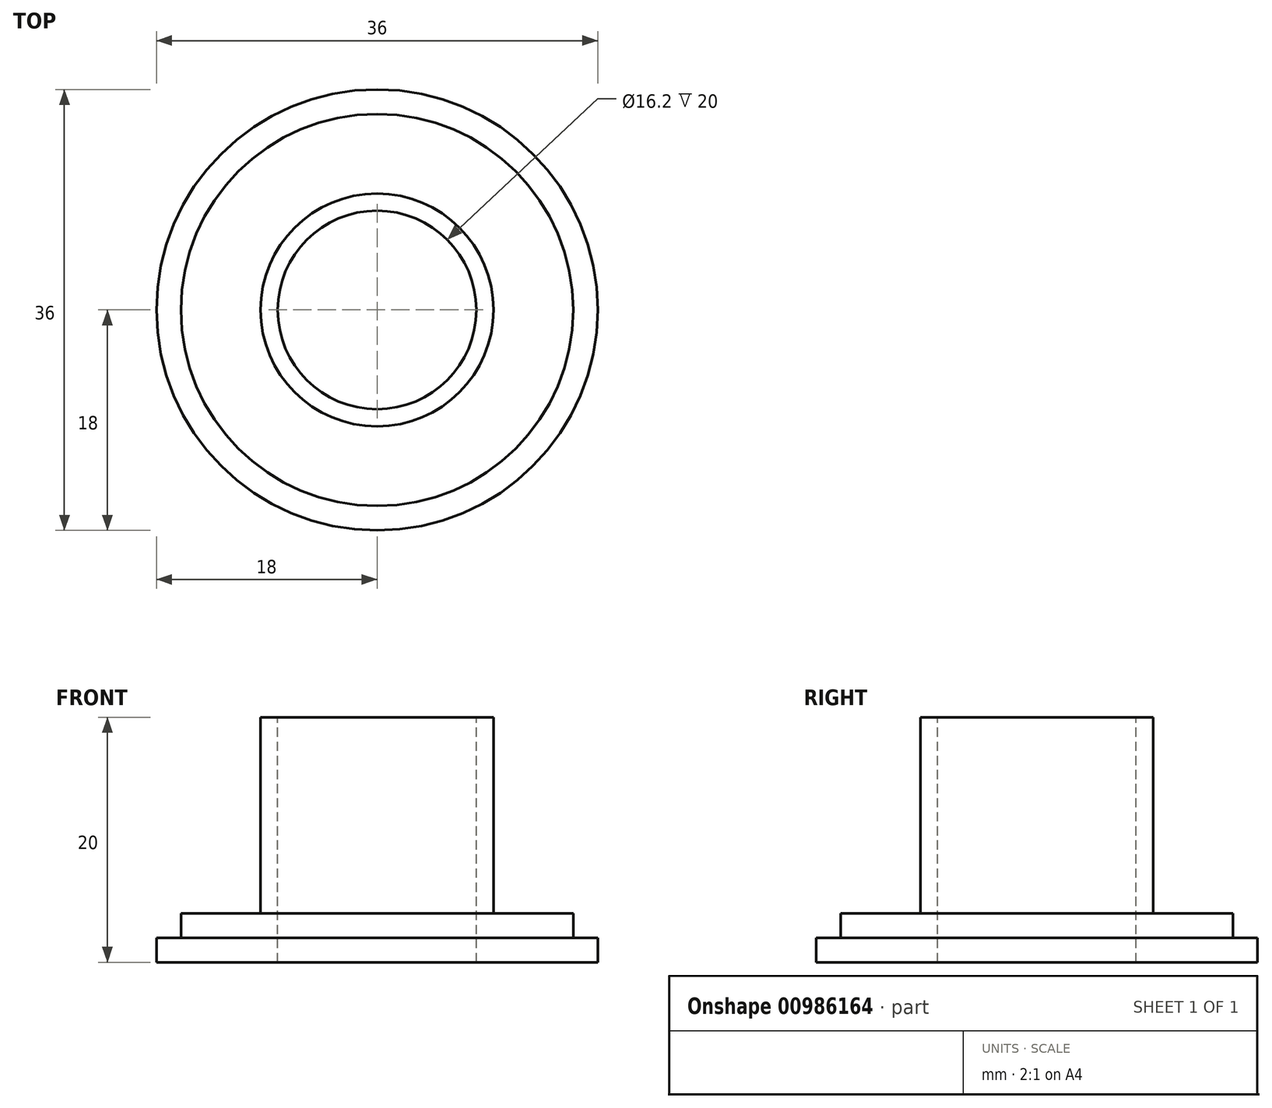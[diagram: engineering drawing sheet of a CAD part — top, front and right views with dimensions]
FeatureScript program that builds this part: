
annotation { "Feature Type Name" : "Feature", "Feature Type Description" : "" }
export const myFeature = defineFeature(function(context is Context, id is Id, definition is map)
    precondition{}
    {
        {
            var Q0;
            Q0=qCreatedBy(makeId("Front.planeOp"),FACE);
            var sketch = newSketch(context, id + "F0", { "sketchPlane" : qUnion([Q0])});
            skLineSegment(sketch, "E0", {"start": v(0, 0) * mm, "end": v(0, 16) * mm});
            skLineSegment(sketch, "E1", {"start": v(0, 16) * mm, "end": v(-9.5, 16) * mm});
            skLineSegment(sketch, "E2", {"start": v(-9.5, 16) * mm, "end": v(-9.5, 0) * mm});
            skLineSegment(sketch, "E3", {"start": v(-9.5, 0) * mm, "end": v(-16, 0) * mm});
            skLineSegment(sketch, "E4", {"start": v(-16, 0) * mm, "end": v(-16, -2) * mm});
            skLineSegment(sketch, "E5", {"start": v(-18, -2) * mm, "end": v(-16, -2) * mm});
            skLineSegment(sketch, "E6", {"start": v(-18, -2) * mm, "end": v(-18, -4) * mm});
            skLineSegment(sketch, "E7", {"start": v(-18, -4) * mm, "end": v(0, -4) * mm});
            skLineSegment(sketch, "E8", {"start": v(0, -4) * mm, "end": v(0, 0) * mm});
            skSolve(sketch);
        }
        {
            var Q0;
            Q0=makeQuery(id+"F0.imprint","IMPRINT",FACE,{"disambiguationData":[TD([[makeQuery(id+"F0.imprint","IMPRINT",EDGE,{"derivedFrom":sQuery(id+"F0.wireOp",EDGE,"E0")}),1.0]])]});
            var Q1;
            Q1=sQuery(id+"F0.wireOp",EDGE,"E8");
            revolve(context, id + "F1", {"surfaceOperationType" : NewSurfaceOperationType.NEW, "entities" : qUnion([Q0]), "axis" : qUnion([Q1]), "revolveType" : RevolveType.FULL});
        }
        {
            var Q0;
            Q0=makeQuery(id+"F1.opRevolve","SWEPT_FACE",FACE,{"disambiguationData":[OSD([sQuery(id+"F0.wireOp",EDGE,"E1")])]});
            var sketch = newSketch(context, id + "F2", { "sketchPlane" : qUnion([Q0])});
            skCircle(sketch, "E9", {"center": v(0, 0) * mm, "radius": 8.1 * mm});
            skSolve(sketch);
        }
        {
            var Q0;
            Q0 = qSketchRegion(id + "F2", true);
            extrude(context, id + "F3", {"entities" : qUnion([Q0]), "operationType" : NewBodyOperationType.REMOVE, "oppositeDirection" : true, "depth" : 40 * mm, "offsetDistance" : 25 * mm});
        }
    });
